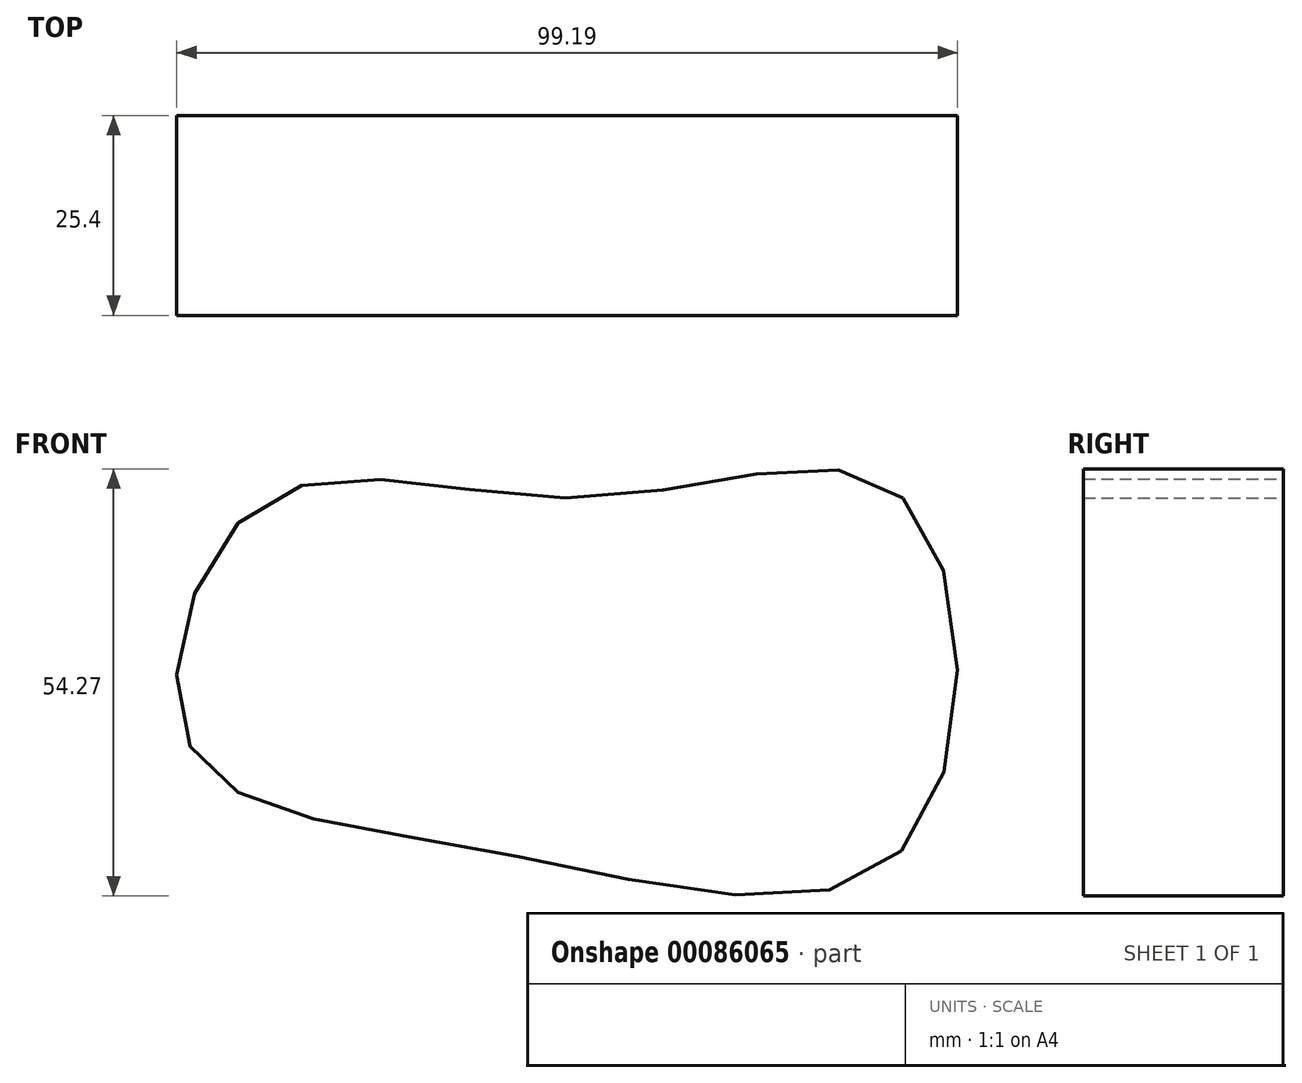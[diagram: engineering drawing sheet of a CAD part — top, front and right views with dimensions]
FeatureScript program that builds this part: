
annotation { "Feature Type Name" : "Feature", "Feature Type Description" : "" }
export const myFeature = defineFeature(function(context is Context, id is Id, definition is map)
    precondition{}
    {
        {
            var Q0;
            Q0=qCreatedBy(makeId("Front.planeOp"),FACE);
            var sketch = newSketch(context, id + "F0", { "sketchPlane" : qUnion([Q0])});
            skPoint(sketch, "E0", {"position": v(-55.55, 58.68) * mm});
            skPoint(sketch, "E1", {"position": v(-64.95, 28.14) * mm});
            skPoint(sketch, "E2", {"position": v(25.8, 59.27) * mm});
            skPoint(sketch, "E3", {"position": v(25.8, 14.63) * mm});
            skPoint(sketch, "E4", {"position": v(-27.65, 14.63) * mm});
            skPoint(sketch, "E5", {"position": v(-13.85, 59.27) * mm});
            skFitSpline(sketch, "E6", {"points": [v(25.8, 59.27) * mm, v(-13.85, 59.27) * mm, v(-55.55, 58.68) * mm, v(-64.95, 28.14) * mm, v(-27.65, 14.63) * mm, v(25.8, 14.63) * mm, v(25.8, 59.27) * mm]});
            skSolve(sketch);
        }
        {
            var Q0;
            Q0=makeQuery(id+"F0.imprint","IMPRINT",FACE,{"disambiguationData":[TD([[makeQuery(id+"F0.imprint","IMPRINT",EDGE,{"derivedFrom":sQuery(id+"F0.wireOp",EDGE,"E6")}),1.0]])]});
            extrude(context, id + "F1", {"entities" : qUnion([Q0]), "depth" : 25.4 * mm});
        }
    });
